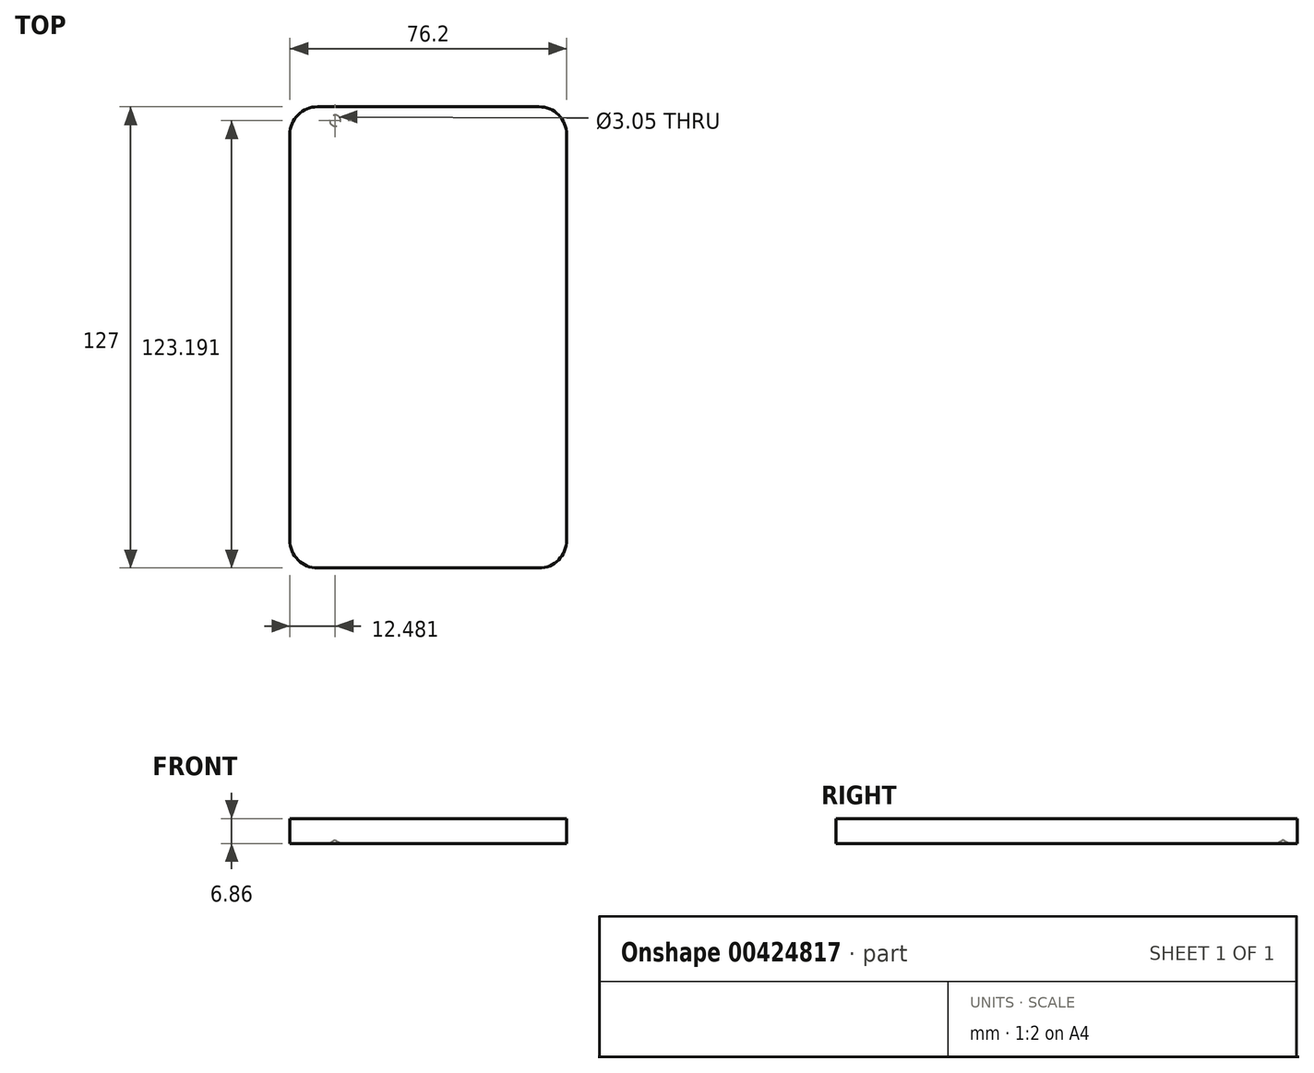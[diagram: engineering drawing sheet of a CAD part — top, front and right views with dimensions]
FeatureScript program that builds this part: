
annotation { "Feature Type Name" : "Feature", "Feature Type Description" : "" }
export const myFeature = defineFeature(function(context is Context, id is Id, definition is map)
    precondition{}
    {
        {
            var Q0;
            Q0=qCreatedBy(makeId("Top.planeOp"),FACE);
            var sketch = newSketch(context, id + "F0", { "sketchPlane" : qUnion([Q0])});
            skLineSegment(sketch, "E0.bottom", {"start": v(-40.77, 57.72) * mm, "end": v(35.43, 57.72) * mm});
            skLineSegment(sketch, "E0.top", {"start": v(-40.77, -69.28) * mm, "end": v(35.43, -69.28) * mm});
            skLineSegment(sketch, "E0.left", {"start": v(-40.77, 57.72) * mm, "end": v(-40.77, -69.28) * mm});
            skLineSegment(sketch, "E0.right", {"start": v(35.43, 57.72) * mm, "end": v(35.43, -69.28) * mm});
            skSolve(sketch);
        }
        {
            var Q0;
            Q0 = qSketchRegion(id + "F0", true);
            var Q1;
            Q1=makeQuery(id+"F0.imprint","IMPRINT",FACE,{"disambiguationData":[TD([[makeQuery(id+"F0.imprint","IMPRINT",EDGE,{"derivedFrom":sQuery(id+"F0.wireOp",EDGE,"E0.bottom")}),-1.0]])]});
            extrude(context, id + "F1", {"entities" : qUnion([Q0, Q1]), "depth" : 6.86 * mm});
        }
        {
            var Q0;
            Q0=makeQuery(id+"F1.opExtrude","SWEPT_EDGE",EDGE,{"disambiguationData":[OSD([sQuery(id+"F0.wireOp",EDGE,"E0.bottom"),sQuery(id+"F0.wireOp",EDGE,"E0.right")])]});
            var Q1;
            Q1=makeQuery(id+"F1.opExtrude","SWEPT_EDGE",EDGE,{"disambiguationData":[OSD([sQuery(id+"F0.wireOp",EDGE,"E0.bottom"),sQuery(id+"F0.wireOp",EDGE,"E0.left")])]});
            var Q2;
            Q2=makeQuery(id+"F1.opExtrude","SWEPT_EDGE",EDGE,{"disambiguationData":[OSD([sQuery(id+"F0.wireOp",EDGE,"E0.top"),sQuery(id+"F0.wireOp",EDGE,"E0.left")])]});
            var Q3;
            Q3=makeQuery(id+"F1.opExtrude","SWEPT_EDGE",EDGE,{"disambiguationData":[OSD([sQuery(id+"F0.wireOp",EDGE,"E0.top"),sQuery(id+"F0.wireOp",EDGE,"E0.right")])]});
            fillet(context, id + "F2", {"entities" : qUnion([Q0, Q1, Q2, Q3]), "radius" : 7.62 * mm, "tangentPropagation" : true, "allowEdgeOverflow" : false});
        }
        {
            var Q0;
            Q0=makeQuery(id+"F1.opExtrude","CAP_FACE",FACE,{"disambiguationData":[OSD([sQuery(id+"F0.wireOp",EDGE,"E0.bottom"),sQuery(id+"F0.wireOp",EDGE,"E0.top"),sQuery(id+"F0.wireOp",EDGE,"E0.left"),sQuery(id+"F0.wireOp",EDGE,"E0.right")])],"isStart":false});
            var sketch = newSketch(context, id + "F3", { "sketchPlane" : qUnion([Q0])});
            skLineSegment(sketch, "E1.bottom", {"start": v(-36.96, 42.48) * mm, "end": v(31.62, 42.48) * mm});
            skLineSegment(sketch, "E1.top", {"start": v(-36.96, -54.04) * mm, "end": v(31.62, -54.04) * mm});
            skLineSegment(sketch, "E1.left", {"start": v(-36.96, 42.48) * mm, "end": v(-36.96, -54.04) * mm});
            skLineSegment(sketch, "E1.right", {"start": v(31.62, 42.48) * mm, "end": v(31.62, -54.04) * mm});
            skPoint(sketch, "E2.centerSnap0", {"position": v(-2.67, -69.28) * mm});
            skSolve(sketch);
        }
        {
            var Q0;
            Q0=makeQuery(id+"F1.opExtrude","CAP_FACE",FACE,{"disambiguationData":[OSD([sQuery(id+"F0.wireOp",EDGE,"E0.bottom"),sQuery(id+"F0.wireOp",EDGE,"E0.top"),sQuery(id+"F0.wireOp",EDGE,"E0.left"),sQuery(id+"F0.wireOp",EDGE,"E0.right")])],"isStart":true});
            var sketch = newSketch(context, id + "F4", { "sketchPlane" : qUnion([Q0])});
            skLineSegment(sketch, "E3", {"start": v(35.43, -50.1) * mm, "end": v(-40.77, -50.1) * mm});
            skLineSegment(sketch, "E4", {"start": v(35.43, -48.15) * mm, "end": v(-40.77, -48.15) * mm});
            skLineSegment(sketch, "E5", {"start": v(35.43, -50.1) * mm, "end": v(35.43, -50.1) * mm});
            skLineSegment(sketch, "E6", {"start": v(27.81, -57.72) * mm, "end": v(-33.15, -57.72) * mm});
            skLineSegment(sketch, "E7", {"start": v(-40.77, -50.1) * mm, "end": v(-40.77, -50.1) * mm});
            skArc(sketch, "E8.filletArc", {"start": v(-40.77, -50.1) * mm, "mid": v(-38.54, -55.49) * mm, "end": v(-33.15, -57.72) * mm});
            skArc(sketch, "E9.filletArc", {"start": v(27.81, -57.72) * mm, "mid": v(33.2, -55.49) * mm, "end": v(35.43, -50.1) * mm});
            skLineSegment(sketch, "E10", {"start": v(34.34, -51.12) * mm, "end": v(-39.67, -51.12) * mm});
            skLineSegment(sketch, "E11", {"start": v(26.72, -56.7) * mm, "end": v(-32.05, -56.7) * mm});
            skArc(sketch, "E12", {"start": v(26.72, -56.7) * mm, "mid": v(31.44, -55.16) * mm, "end": v(34.34, -51.12) * mm});
            skArc(sketch, "E13", {"start": v(-39.67, -51.12) * mm, "mid": v(-36.78, -55.16) * mm, "end": v(-32.05, -56.7) * mm});
            skPoint(sketch, "E14", {"position": v(-28.29, -53.91) * mm});
            skCircle(sketch, "E15", {"center": v(-28.29, -53.91) * mm, "radius": 1.57 * mm});
            skPoint(sketch, "E16", {"position": v(-25.63, -53.91) * mm});
            skCircle(sketch, "E17", {"center": v(-25.63, -53.91) * mm, "radius": 0.1 * mm});
            skCircle(sketch, "E18", {"center": v(-24.4, -53.91) * mm, "radius": 0.27 * mm});
            skSolve(sketch);
        }
        {
            var Q0;
            Q0=sQuery(id+"F4.wireOp",VERTEX,"E14");
            var Q1;
            Q1=makeQuery(id+"F1.opExtrude","SWEPT_BODY",BODY,{"disambiguationData":[OSD([sQuery(id+"F0.wireOp",EDGE,"E0.bottom"),sQuery(id+"F0.wireOp",EDGE,"E0.top"),sQuery(id+"F0.wireOp",EDGE,"E0.left"),sQuery(id+"F0.wireOp",EDGE,"E0.right")])]});
            hole(context, id + "F5", {"style" : HoleStyle.SIMPLE, "endStyle" : HoleEndStyle.BLIND, "holeDiameter" : 3.05 * mm, "majorDiameter" : 6.35 * mm, "holeDepth" : 0.05 * mm, "isTappedThrough" : true, "tappedDepth" : 12.7 * mm, "tapClearance" : 3, "locations" : qUnion([Q0]), "scope" : qUnion([Q1])});
        }
    });
